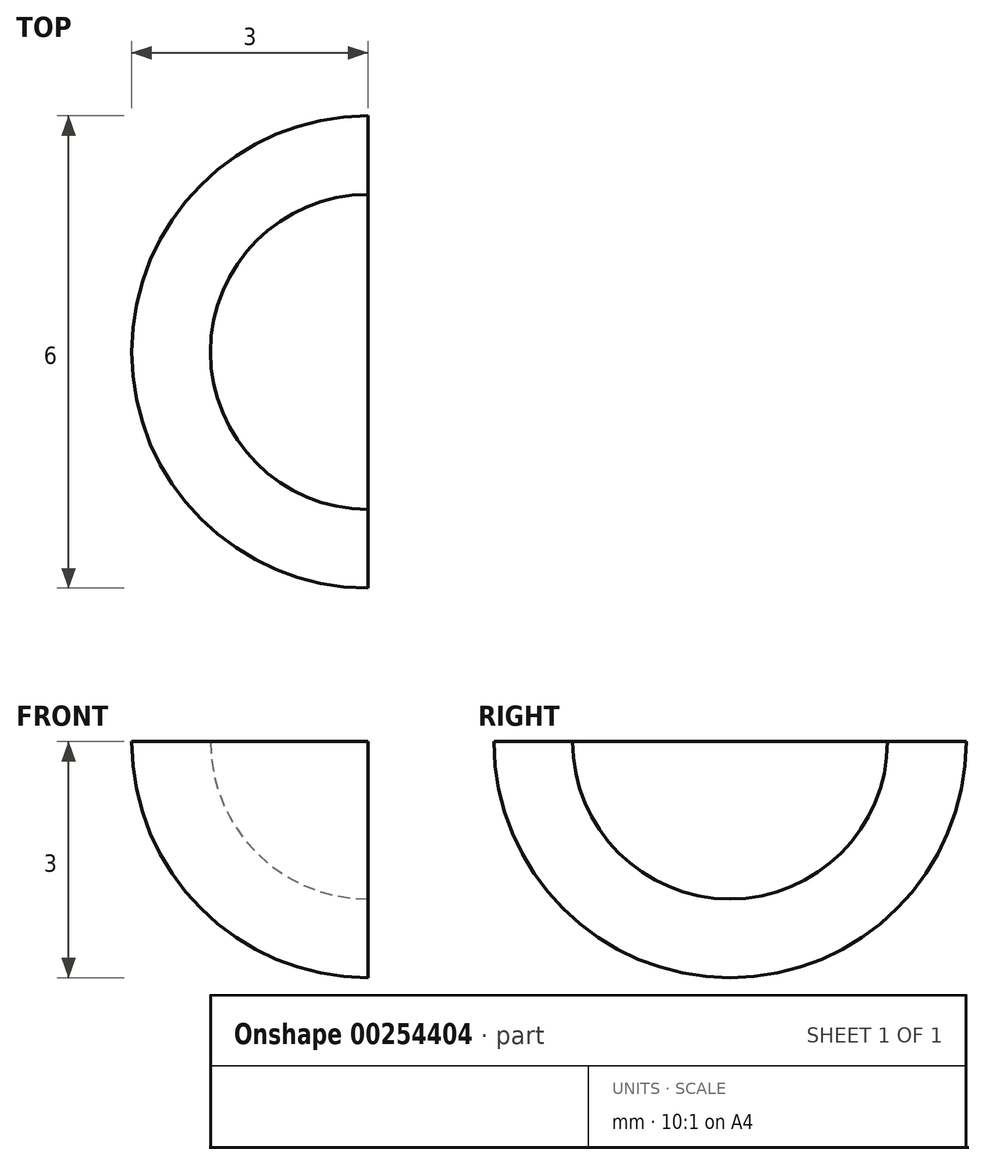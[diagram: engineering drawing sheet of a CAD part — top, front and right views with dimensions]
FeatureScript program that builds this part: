
annotation { "Feature Type Name" : "Feature", "Feature Type Description" : "" }
export const myFeature = defineFeature(function(context is Context, id is Id, definition is map)
    precondition{}
    {
        {
            var Q0;
            Q0=qCreatedBy(makeId("Front.planeOp"),FACE);
            var sketch = newSketch(context, id + "F0", { "sketchPlane" : qUnion([Q0])});
            skArc(sketch, "E0", {"start": v(0, -3) * mm, "mid": v(3, 0) * mm, "end": v(0, 3) * mm});
            skArc(sketch, "E1", {"start": v(0, -2) * mm, "mid": v(2, 0) * mm, "end": v(0, 2) * mm});
            skLineSegment(sketch, "E2", {"start": v(0, 3) * mm, "end": v(0, -3) * mm});
            skSolve(sketch);
        }
        {
            var Q0;
            {var subQ0=sQuery(id+"F0.wireOp",EDGE,"E0");Q0=makeQuery(id+"F0.imprint","IMPRINT",FACE,{"disambiguationData":[TD([[makeQuery(id+"F0.imprint","IMPRINT",EDGE,{"derivedFrom":subQ0}),1.0]])]});}
            var Q1;
            Q1=sQuery(id+"F0.wireOp",EDGE,"E2");
            revolve(context, id + "F1", {"entities" : qUnion([Q0]), "axis" : qUnion([Q1]), "revolveType" : RevolveType.FULL});
        }
        {
            var Q0;
            Q0=qCreatedBy(makeId("Front.planeOp"),FACE);
            var sketch = newSketch(context, id + "F2", { "sketchPlane" : qUnion([Q0])});
            skLineSegment(sketch, "E3.bottom", {"start": v(-5.18, 0) * mm, "end": v(6.52, 0) * mm});
            skLineSegment(sketch, "E3.top", {"start": v(-5.18, 3.63) * mm, "end": v(6.52, 3.63) * mm});
            skLineSegment(sketch, "E3.left", {"start": v(-5.18, 0) * mm, "end": v(-5.18, 3.63) * mm});
            skLineSegment(sketch, "E3.right", {"start": v(6.52, 0) * mm, "end": v(6.52, 3.63) * mm});
            skSolve(sketch);
        }
        {
            var Q0;
            Q0=makeQuery(id+"F2.imprint","IMPRINT",FACE,{"disambiguationData":[TD([[makeQuery(id+"F2.imprint","IMPRINT",EDGE,{"derivedFrom":sQuery(id+"F2.wireOp",EDGE,"E3.bottom")}),1.0]])]});
            extrude(context, id + "F3", {"entities" : qUnion([Q0]), "operationType" : NewBodyOperationType.REMOVE, "endBound" : BoundingType.SYMMETRIC, "oppositeDirection" : true, "depth" : 25 * mm});
        }
        {
            var Q0;
            Q0=qCreatedBy(makeId("Right.planeOp"),FACE);
            var sketch = newSketch(context, id + "F4", { "sketchPlane" : qUnion([Q0])});
            skLineSegment(sketch, "E4.bottom", {"start": v(-6.18, 2.11) * mm, "end": v(6.88, 2.11) * mm});
            skLineSegment(sketch, "E4.top", {"start": v(-6.18, -5.47) * mm, "end": v(6.88, -5.47) * mm});
            skLineSegment(sketch, "E4.left", {"start": v(-6.18, 2.11) * mm, "end": v(-6.18, -5.47) * mm});
            skLineSegment(sketch, "E4.right", {"start": v(6.88, 2.11) * mm, "end": v(6.88, -5.47) * mm});
            skSolve(sketch);
        }
        {
            var Q0;
            Q0=makeQuery(id+"F4.imprint","IMPRINT",FACE,{"disambiguationData":[TD([[makeQuery(id+"F4.imprint","IMPRINT",EDGE,{"derivedFrom":sQuery(id+"F4.wireOp",EDGE,"E4.bottom")}),-1.0]])]});
            extrude(context, id + "F5", {"entities" : qUnion([Q0]), "operationType" : NewBodyOperationType.REMOVE, "depth" : 25 * mm});
        }
    });
